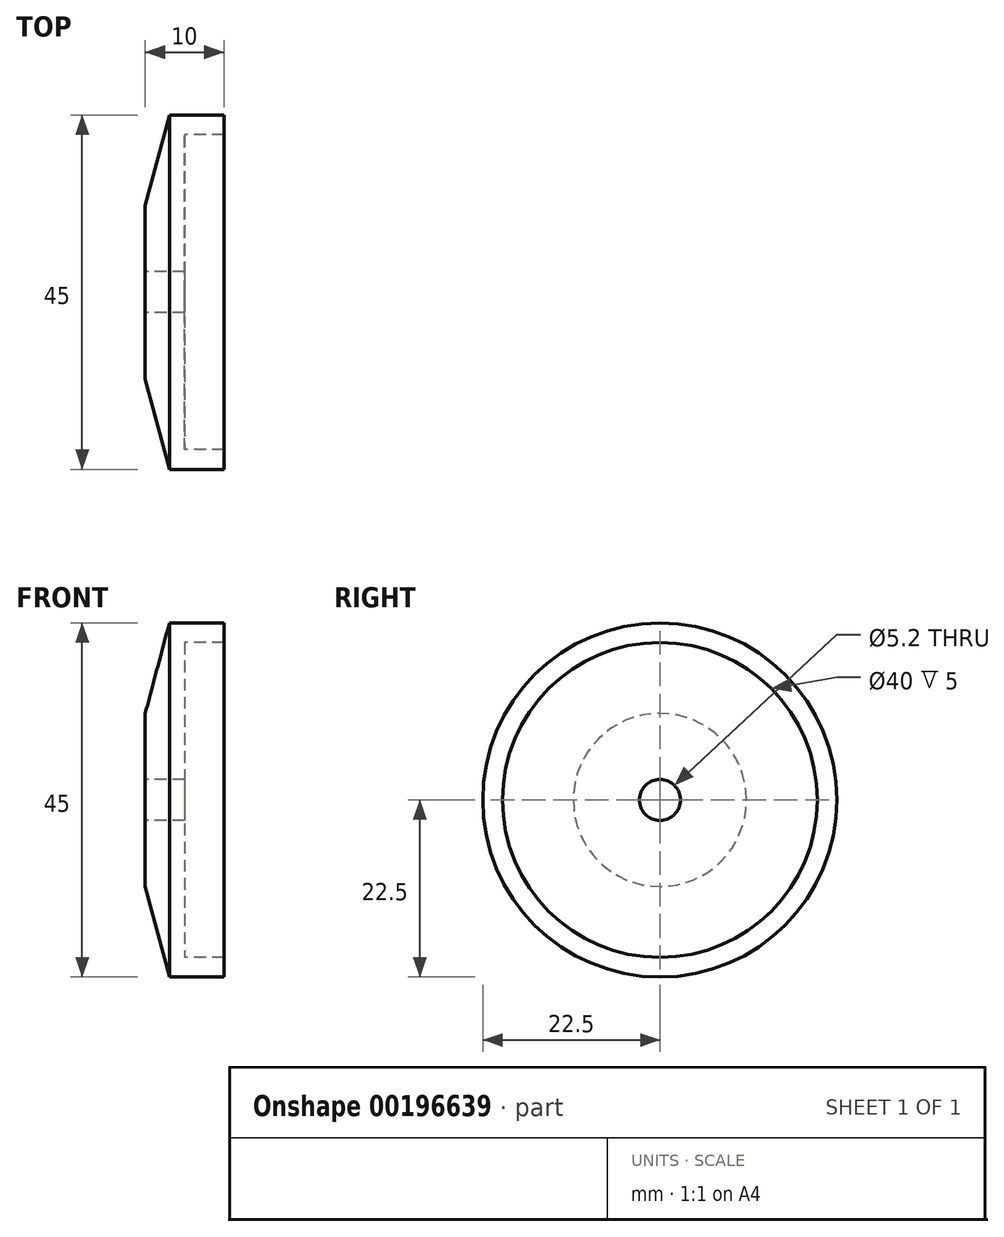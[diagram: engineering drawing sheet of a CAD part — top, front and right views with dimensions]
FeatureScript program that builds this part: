
annotation { "Feature Type Name" : "Feature", "Feature Type Description" : "" }
export const myFeature = defineFeature(function(context is Context, id is Id, definition is map)
    precondition{}
    {
        {
            var Q0;
            Q0=qCreatedBy(makeId("Front.planeOp"),FACE);
            var sketch = newSketch(context, id + "F0", { "sketchPlane" : qUnion([Q0])});
            skLineSegment(sketch, "E0", {"start": v(0, 2.6) * mm, "end": v(0, 11) * mm});
            skLineSegment(sketch, "E1", {"start": v(0, 11) * mm, "end": v(3.08, 22.5) * mm});
            skLineSegment(sketch, "E2", {"start": v(3.08, 22.5) * mm, "end": v(10, 22.5) * mm});
            skLineSegment(sketch, "E3", {"start": v(10, 22.5) * mm, "end": v(10, 20) * mm});
            skLineSegment(sketch, "E4", {"start": v(10, 20) * mm, "end": v(5, 20) * mm});
            skLineSegment(sketch, "E5", {"start": v(5, 20) * mm, "end": v(5, 2.6) * mm});
            skLineSegment(sketch, "E6", {"start": v(5, 2.6) * mm, "end": v(0, 2.6) * mm});
            skLineSegment(sketch, "E7", {"start": v(0, 0) * mm, "end": v(65.65, 0) * mm, "construction": true});
            skSolve(sketch);
        }
        {
            var Q0;
            Q0=makeQuery(id+"F0.imprint","IMPRINT",FACE,{"disambiguationData":[TD([[makeQuery(id+"F0.imprint","IMPRINT",EDGE,{"derivedFrom":sQuery(id+"F0.wireOp",EDGE,"E0")}),-1.0]])]});
            var Q1;
            Q1=sQuery(id+"F0.wireOp",EDGE,"E7");
            revolve(context, id + "F1", {"entities" : qUnion([Q0]), "axis" : qUnion([Q1]), "revolveType" : RevolveType.FULL});
        }
    });
